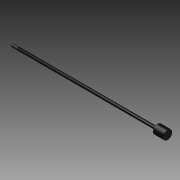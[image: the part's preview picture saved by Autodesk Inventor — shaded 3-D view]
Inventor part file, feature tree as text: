
AUTODESK INVENTOR PART (.ipt)
format: ipt  version: 2011 SP1 (Build 150282100, 282)  size: 117,248 bytes
history: native  units: in
note: dims shown in document units (in); Inventor stores cm internally (conversion verified against a paired STEP export)
features: other x70, revolve x3, sketch x3, thread x1
ambient origin geometry x8: Origin, YZ Plane, XZ Plane, XY Plane, X Axis, Y Axis, Z Axis, Center Point
bodies: Solid1 (feature_tree)
feature tree (77):
  revolve  "Revolution1"  Angle=360.0deg
  revolve  "Revolution2"  Angle=360.0deg
  thread  "Thread1"  [1 undecoded]
  revolve  "Revolution3"  [1 undecoded]
  other  "dia1_XY"
  other  "dia1_YZ"
  other  "dia1_ZX"
  other  "dia1_X"
  other  "dia1_Y"
  other  "dia1_Z"
  other  "dia1_Center"
  other  "dia12_XY"
  other  "dia12_YZ"
  other  "dia12_ZX"
  other  "dia12_X"
  other  "dia12_Y"
  other  "dia12_Z"
  other  "dia12_Center"
  other  "dia2_XY"
  other  "dia2_YZ"
  other  "dia2_ZX"
  other  "dia2_X"
  other  "dia2_Y"
  other  "dia2_Z"
  other  "dia2_Center"
  other  "dia22_XY"
  other  "dia22_YZ"
  other  "dia22_ZX"
  other  "dia22_X"
  other  "dia22_Y"
  other  "dia22_Z"
  other  "dia22_Center"
  other  "rl1_XY"
  other  "rl1_YZ"
  other  "rl1_ZX"
  other  "rl1_X"
  other  "rl1_Y"
  other  "rl1_Z"
  other  "rl1_Center"
  other  "rl2_XY"
  other  "rl2_YZ"
  other  "rl2_ZX"
  other  "rl2_X"
  other  "rl2_Y"
  other  "rl2_Z"
  other  "rl2_Center"
  other  "rod_cp_XY"
  other  "rod_cp_YZ"
  other  "rod_cp_ZX"
  other  "rod_cp_X"
  other  "rod_cp_Y"
  other  "rod_cp_Z"
  other  "rod_cp_Center"
  other  "thd1_XY"
  other  "thd1_YZ"
  other  "thd1_ZX"
  other  "thd1_X"
  other  "thd1_Y"
  other  "thd1_Z"
  other  "thd1_Center"
  other  "thd2_XY"
  other  "thd2_YZ"
  other  "thd2_ZX"
  other  "thd2_X"
  other  "thd2_Y"
  other  "thd2_Z"
  other  "thd2_Center"
  other  "to_rod_clevis_XY"
  other  "to_rod_clevis_YZ"
  other  "to_rod_clevis_ZX"
  other  "to_rod_clevis_X"
  other  "to_rod_clevis_Y"
  other  "to_rod_clevis_Z"
  other  "to_rod_clevis_Center"
  sketch  "Sketch_1"  dims[d0=360.0deg d1=360.0deg]
  sketch  "Sketch_3"  dims[d2=0.4787in d3=0.0in d4=360.0deg d5=0.0in d6=0.0in d7=0.0in]
  sketch  "Sketch_30"
note: 2 required parameter values undecoded (feature->parameter linkage not recoverable at this tier; creation-order binding heuristic only, values carry confidence <= 0.55)
